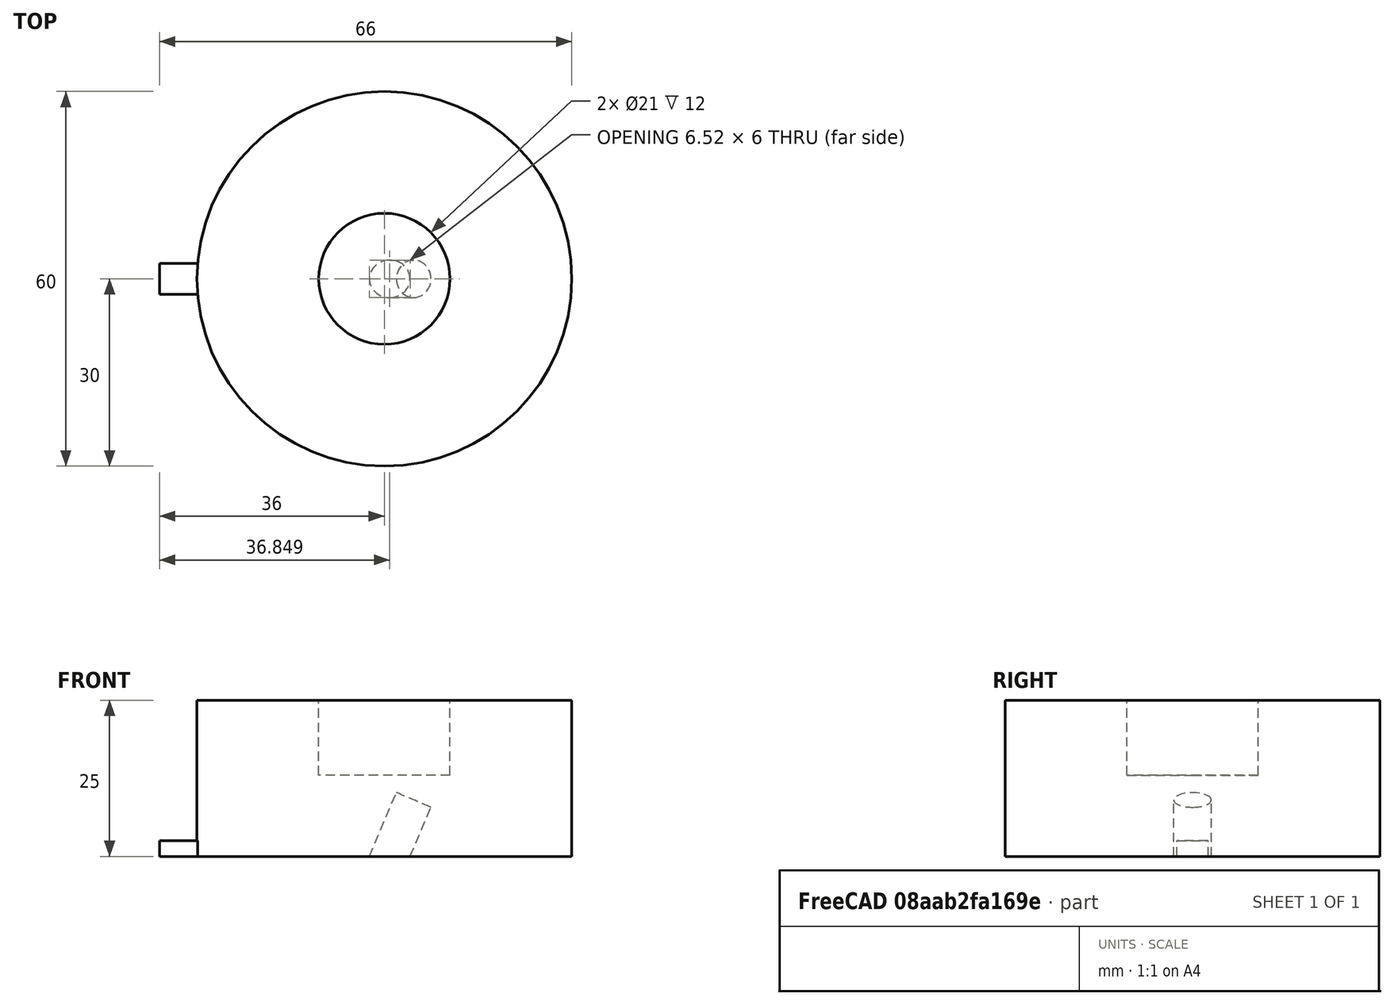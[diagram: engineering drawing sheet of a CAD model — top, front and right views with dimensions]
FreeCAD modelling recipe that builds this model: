
FCSTD DOCUMENT  (FreeCAD 0.16R6712 (Git))
Label: i-seasons1
License: All rights reserved
LicenseURL: http://en.wikipedia.org/wiki/All_rights_reserved
objects: Part::Cylinder×3, Part::Cut×2, Part::Box×1, Part::MultiFuse×1, Part::Feature×1
note: 8 computed .brp shape members not serialized (recipe doc carries the construction recipe); baked Part::Feature solids carry a one-line shape summary decoded from their .brp

FEATURE [Part::Cylinder] Cylinder
  Angle = 360
  Height = 25
  Radius = 30
FEATURE [Part::Cylinder] Cylinder001  label="Cylinder hole"
  Angle = 360
  Height = 12
  Placement = pos=(0,0,13) rot=(0,0,1;0rad)
  Radius = 10.5
FEATURE [Part::Cylinder] Cylinder002  label="Cylinder earth axis"
  Angle = 360
  Height = 12
  Placement = pos=(0,0,-2) rot=(0,1,0;0.401426rad)
  Radius = 3
FEATURE [Part::Box] Box  label="Position"
  Height = 2.5
  Length = 30
  Placement = pos=(-6,-2.5,2.5) rot=(0,1,0;3.14159rad)
  Width = 5
FEATURE [Part::MultiFuse] Fusion
  Shapes = -> [Cylinder,Box]
FEATURE [Part::Cut] Cut
  Base = -> Fusion
  Tool = -> Cylinder002
FEATURE [Part::Cut] Cut001  label="Piece 1"
  Base = -> Cut
  Tool = -> Cylinder001
FEATURE [Part::Feature] Cut001001  label="piece to print"
  shape: bbox 66 x 60 x 27.34 mm, 11 faces (baked)
